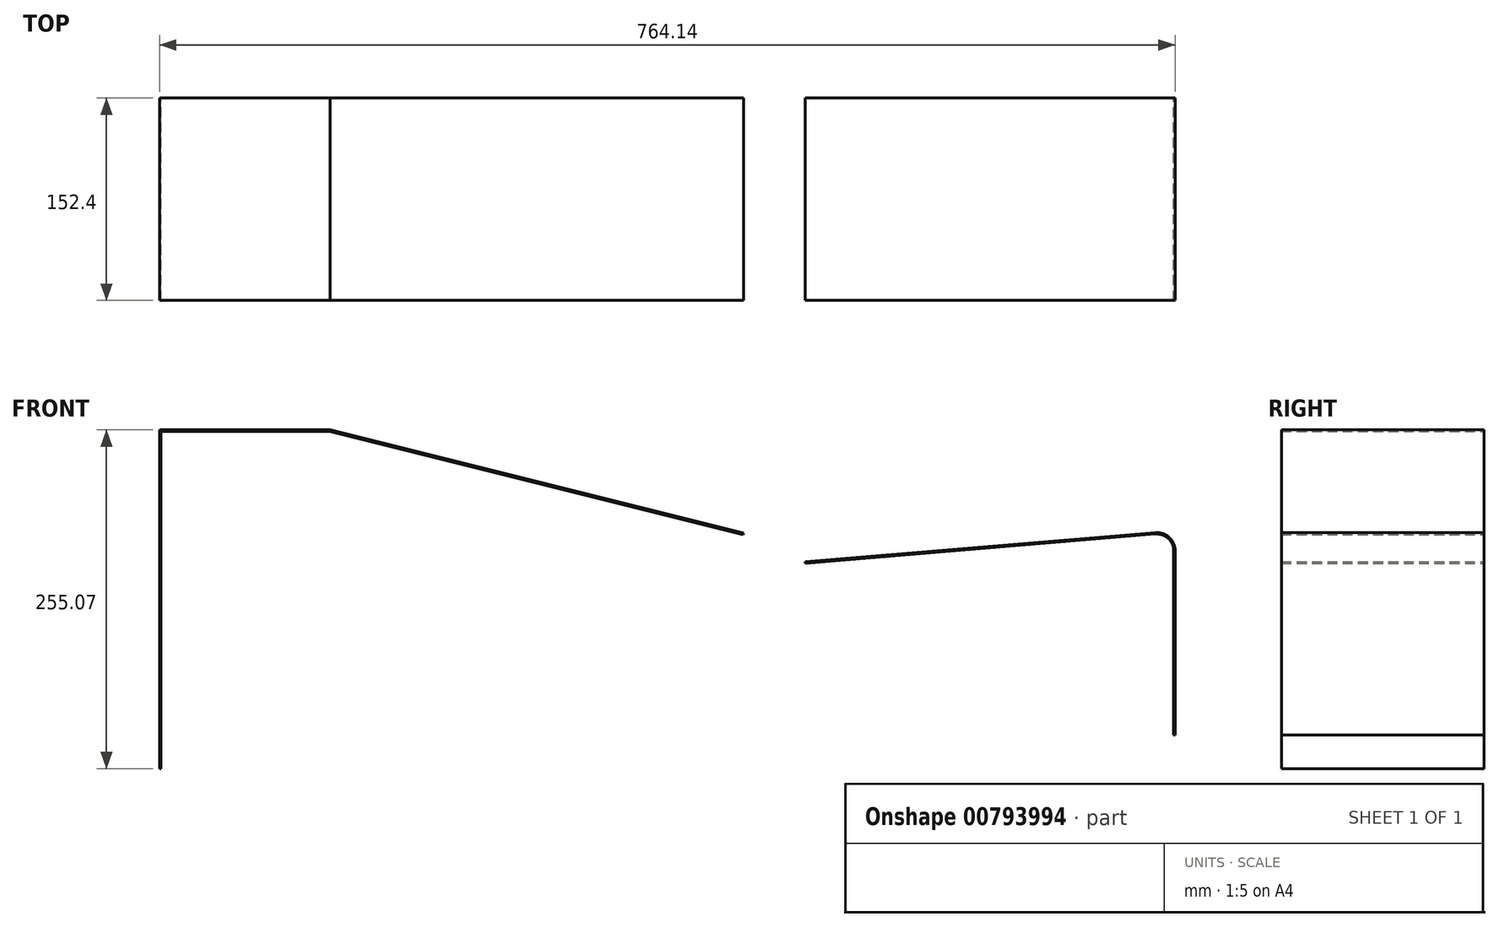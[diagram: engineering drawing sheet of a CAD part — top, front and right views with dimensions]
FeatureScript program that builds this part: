
annotation { "Feature Type Name" : "Feature", "Feature Type Description" : "" }
export const myFeature = defineFeature(function(context is Context, id is Id, definition is map)
    precondition{}
    {
        {
            var Q0;
            Q0=qCreatedBy(makeId("Front.planeOp"),FACE);
            var sketch = newSketch(context, id + "F0", { "sketchPlane" : qUnion([Q0])});
            skLineSegment(sketch, "E0", {"start": v(0, 0) * mm, "end": v(0, -254) * mm});
            skLineSegment(sketch, "E1", {"start": v(0, 0) * mm, "end": v(127, 0) * mm});
            skLineSegment(sketch, "E2", {"start": v(127, 0) * mm, "end": v(437.96, -77.74) * mm});
            skLineSegment(sketch, "E3", {"start": v(457.2, -102.38) * mm, "end": v(457.2, -102.38) * mm});
            skLineSegment(sketch, "E4", {"start": v(484.7, -99.3) * mm, "end": v(748.25, -77.35) * mm});
            skLineSegment(sketch, "E5", {"start": v(179.09, -101.6) * mm, "end": v(985.38, -101.6) * mm, "construction": true});
            skPoint(sketch, "E6.visualSharp", {"position": v(457.2, -101.6) * mm});
            skPoint(sketch, "E7.visualSharp", {"position": v(457.2, -82.55) * mm});
            skLineSegment(sketch, "E8", {"start": v(762, -90) * mm, "end": v(762, -228.6) * mm});
            skPoint(sketch, "E9.visualSharp", {"position": v(762, -76.2) * mm});
            skArc(sketch, "E9.filletArc", {"start": v(762, -90) * mm, "mid": v(757.9, -80.66) * mm, "end": v(748.25, -77.35) * mm});
            skLineSegment(sketch, "E10.0", {"start": v(-1.07, 1.07) * mm, "end": v(-1.07, -254) * mm});
            skLineSegment(sketch, "E10.1", {"start": v(-1.07, 1.07) * mm, "end": v(127.13, 1.07) * mm});
            skLineSegment(sketch, "E10.2", {"start": v(127.13, 1.07) * mm, "end": v(438.22, -76.7) * mm});
            skLineSegment(sketch, "E10.4", {"start": v(458.27, -102.38) * mm, "end": v(458.27, -102.38) * mm});
            skLineSegment(sketch, "E10.5", {"start": v(763.07, -90) * mm, "end": v(763.07, -228.6) * mm});
            skArc(sketch, "E10.6", {"start": v(763.07, -90) * mm, "mid": v(758.62, -79.87) * mm, "end": v(748.16, -76.28) * mm});
            skLineSegment(sketch, "E10.7", {"start": v(484.62, -98.24) * mm, "end": v(748.16, -76.28) * mm});
            skLineSegment(sketch, "E11", {"start": v(-1.07, -254) * mm, "end": v(0, -254) * mm});
            skLineSegment(sketch, "E12", {"start": v(763.07, -228.6) * mm, "end": v(762, -228.6) * mm});
            skLineSegment(sketch, "E13", {"start": v(437.96, -77.74) * mm, "end": v(438.22, -76.7) * mm});
            skLineSegment(sketch, "E14", {"start": v(484.7, -99.3) * mm, "end": v(484.62, -98.24) * mm});
            skSolve(sketch);
        }
        {
            var Q0;
            Q0 = qSketchRegion(id + "F0", true);
            extrude(context, id + "F1", {"entities" : qUnion([Q0]), "depth" : 152.4 * mm, "offsetDistance" : 25.4 * mm});
        }
    });
